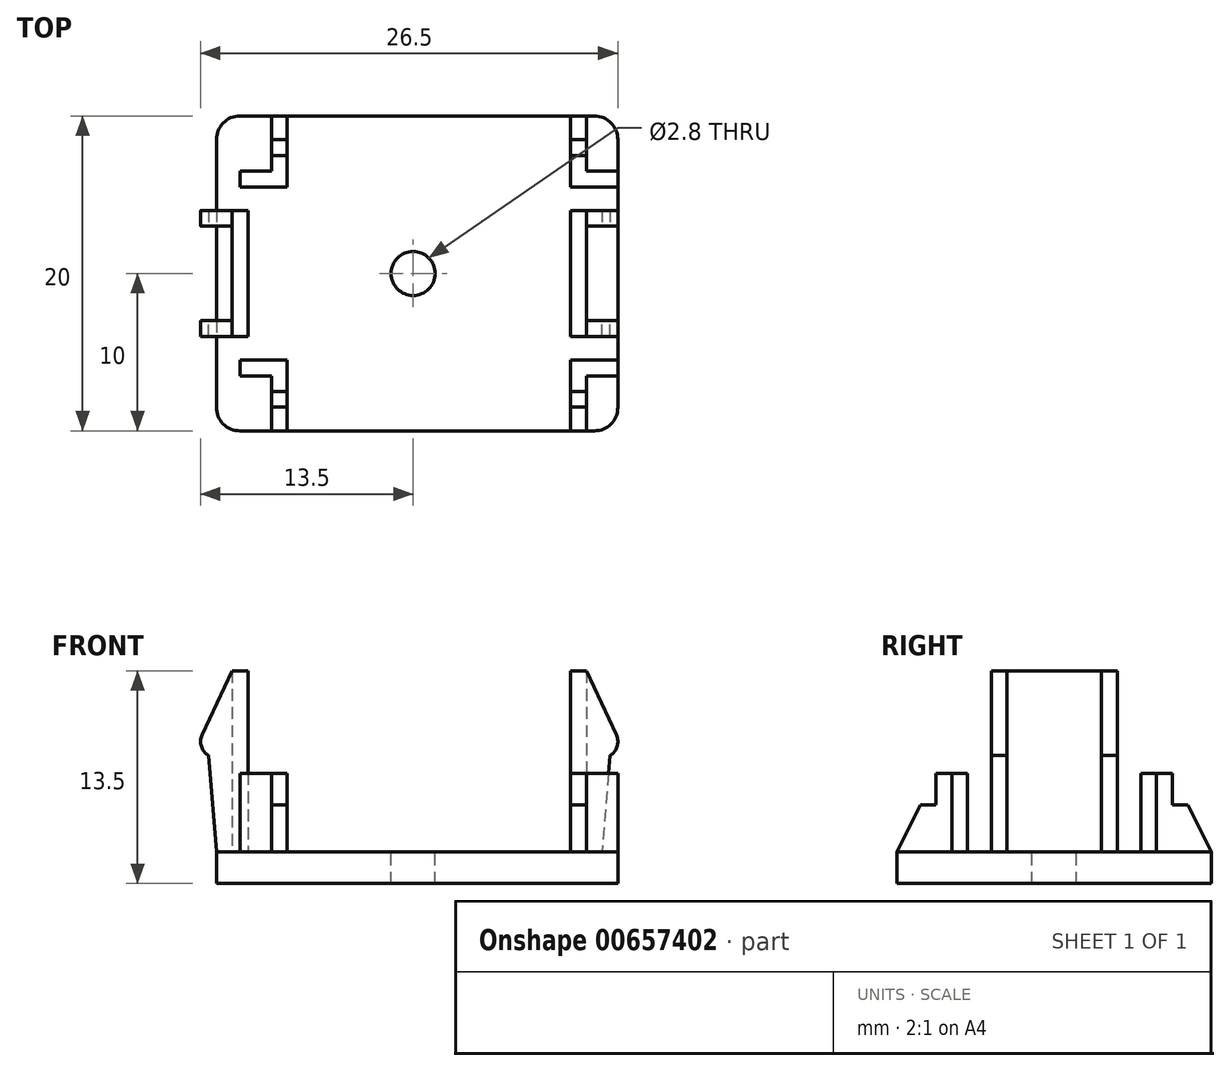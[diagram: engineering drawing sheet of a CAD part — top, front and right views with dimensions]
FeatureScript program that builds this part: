
annotation { "Feature Type Name" : "Feature", "Feature Type Description" : "" }
export const myFeature = defineFeature(function(context is Context, id is Id, definition is map)
    precondition{}
    {
        {
            var Q0;
            Q0=qCreatedBy(makeId("Top.planeOp"),FACE);
            var sketch = newSketch(context, id + "F0", { "sketchPlane" : qUnion([Q0])});
            skLineSegment(sketch, "E0", {"start": v(-7.5, 10) * mm, "end": v(-7.5, 5.5) * mm});
            skLineSegment(sketch, "E1", {"start": v(-7.5, 5.5) * mm, "end": v(-10.5, 5.5) * mm});
            skLineSegment(sketch, "E2", {"start": v(-10.5, 5.5) * mm, "end": v(-10.5, 6.5) * mm});
            skLineSegment(sketch, "E3", {"start": v(-10.5, 6.5) * mm, "end": v(-8.5, 6.5) * mm});
            skLineSegment(sketch, "E4", {"start": v(-8.5, 6.5) * mm, "end": v(-8.5, 10) * mm});
            skLineSegment(sketch, "E5", {"start": v(-8.5, 10) * mm, "end": v(-7.5, 10) * mm});
            skLineSegment(sketch, "E6", {"start": v(-13, 4) * mm, "end": v(-10, 4) * mm});
            skLineSegment(sketch, "E7", {"start": v(-10, 4) * mm, "end": v(-10, 0) * mm});
            skLineSegment(sketch, "E8", {"start": v(-10, 0) * mm, "end": v(-11, 0) * mm});
            skLineSegment(sketch, "E9", {"start": v(-11, 0) * mm, "end": v(-11, 3) * mm});
            skLineSegment(sketch, "E10", {"start": v(-11, 3) * mm, "end": v(-13, 3) * mm});
            skLineSegment(sketch, "E11", {"start": v(-13, 3) * mm, "end": v(-13, 4) * mm});
            skLineSegment(sketch, "E12", {"start": v(10.5, 10) * mm, "end": v(10.5, 5.5) * mm});
            skPoint(sketch, "E12.startSnap0", {"position": v(-8, 10) * mm});
            skLineSegment(sketch, "E13", {"start": v(10.5, 5.5) * mm, "end": v(13.5, 5.5) * mm});
            skLineSegment(sketch, "E14", {"start": v(13.5, 5.5) * mm, "end": v(13.5, 6.5) * mm});
            skLineSegment(sketch, "E15", {"start": v(13.5, 6.5) * mm, "end": v(11.5, 6.5) * mm});
            skLineSegment(sketch, "E16", {"start": v(11.5, 6.5) * mm, "end": v(11.5, 10) * mm});
            skLineSegment(sketch, "E17", {"start": v(11.5, 10) * mm, "end": v(10.5, 10) * mm});
            skLineSegment(sketch, "E18", {"start": v(10.5, 4) * mm, "end": v(10.5, 0) * mm});
            skLineSegment(sketch, "E19", {"start": v(10.5, 0) * mm, "end": v(11.5, 0) * mm});
            skLineSegment(sketch, "E20", {"start": v(11.5, 0) * mm, "end": v(11.5, 3) * mm});
            skLineSegment(sketch, "E21", {"start": v(11.5, 3) * mm, "end": v(13.5, 3) * mm});
            skLineSegment(sketch, "E22", {"start": v(13.5, 3) * mm, "end": v(13.5, 4) * mm});
            skLineSegment(sketch, "E23", {"start": v(13.5, 4) * mm, "end": v(10.5, 4) * mm});
            skSolve(sketch);
        }
        {
            var Q0;
            Q0=makeQuery(id+"F0.imprint","IMPRINT",FACE,{"disambiguationData":[TD([[makeQuery(id+"F0.imprint","IMPRINT",EDGE,{"derivedFrom":sQuery(id+"F0.wireOp",EDGE,"E0")}),-1.0]])]});
            var Q1;
            Q1=makeQuery(id+"F0.imprint","IMPRINT",FACE,{"disambiguationData":[TD([[makeQuery(id+"F0.imprint","IMPRINT",EDGE,{"derivedFrom":sQuery(id+"F0.wireOp",EDGE,"E6")}),-1.0]])]});
            var Q2;
            Q2=makeQuery(id+"F0.imprint","IMPRINT",FACE,{"disambiguationData":[TD([[makeQuery(id+"F0.imprint","IMPRINT",EDGE,{"derivedFrom":sQuery(id+"F0.wireOp",EDGE,"E12")}),1.0]])]});
            var Q3;
            Q3=makeQuery(id+"F0.imprint","IMPRINT",FACE,{"disambiguationData":[TD([[makeQuery(id+"F0.imprint","IMPRINT",EDGE,{"derivedFrom":sQuery(id+"F0.wireOp",EDGE,"E18")}),1.0]])]});
            extrude(context, id + "F1", {"entities" : qUnion([Q0, Q1, Q2, Q3]), "depth" : 11.5 * mm});
        }
        {
            var Q0;
            Q0=makeQuery(id+"F1.opExtrude","SWEPT_FACE",FACE,{"disambiguationData":[OSD([sQuery(id+"F0.wireOp",EDGE,"E10")])]});
            var sketch = newSketch(context, id + "F2", { "sketchPlane" : qUnion([Q0])});
            skArc(sketch, "E24", {"start": v(-12.9, 7.42) * mm, "mid": v(-12.95, 6.7) * mm, "end": v(-12.5, 6.13) * mm});
            skArc(sketch, "E25", {"start": v(13.4, 7.42) * mm, "mid": v(13.45, 6.7) * mm, "end": v(13, 6.13) * mm});
            skLineSegment(sketch, "E26", {"start": v(-12, 0) * mm, "end": v(-12.5, 6.13) * mm});
            skLineSegment(sketch, "E27", {"start": v(-12, 0) * mm, "end": v(-13, 0) * mm});
            skLineSegment(sketch, "E28", {"start": v(-13, 0) * mm, "end": v(-13, 7) * mm});
            skLineSegment(sketch, "E29", {"start": v(-11, 11.5) * mm, "end": v(-12.9, 7.42) * mm});
            skLineSegment(sketch, "E30", {"start": v(-11, 11.5) * mm, "end": v(-13, 11.5) * mm});
            skLineSegment(sketch, "E31", {"start": v(-13, 11.5) * mm, "end": v(-13, 7) * mm});
            skLineSegment(sketch, "E32", {"start": v(12.5, 0) * mm, "end": v(13, 6.13) * mm});
            skLineSegment(sketch, "E33", {"start": v(12.5, 0) * mm, "end": v(13.5, 0) * mm});
            skLineSegment(sketch, "E34", {"start": v(13.5, 0) * mm, "end": v(13.5, 7) * mm});
            skLineSegment(sketch, "E35", {"start": v(11.5, 11.5) * mm, "end": v(13.4, 7.42) * mm});
            skLineSegment(sketch, "E36", {"start": v(11.5, 11.5) * mm, "end": v(13.5, 11.5) * mm});
            skLineSegment(sketch, "E37", {"start": v(13.5, 11.5) * mm, "end": v(13.5, 7) * mm});
            skSolve(sketch);
        }
        {
            var Q0;
            {var subQ0=sQuery(id+"F2.wireOp",EDGE,"E29");Q0=makeQuery(id+"F2.imprint","IMPRINT",FACE,{"disambiguationData":[TD([[makeQuery(id+"F2.imprint","IMPRINT",EDGE,{"derivedFrom":subQ0}),-1.0]])]});}
            var Q1;
            {var subQ0=sQuery(id+"F2.wireOp",EDGE,"E26");Q1=makeQuery(id+"F2.imprint","IMPRINT",FACE,{"disambiguationData":[TD([[makeQuery(id+"F2.imprint","IMPRINT",EDGE,{"derivedFrom":subQ0}),1.0]])]});}
            var Q2;
            {var subQ0=sQuery(id+"F2.wireOp",EDGE,"E35");Q2=makeQuery(id+"F2.imprint","IMPRINT",FACE,{"disambiguationData":[TD([[makeQuery(id+"F2.imprint","IMPRINT",EDGE,{"derivedFrom":subQ0}),1.0]])]});}
            var Q3;
            {var subQ0=sQuery(id+"F2.wireOp",EDGE,"E32");Q3=makeQuery(id+"F2.imprint","IMPRINT",FACE,{"disambiguationData":[TD([[makeQuery(id+"F2.imprint","IMPRINT",EDGE,{"derivedFrom":subQ0}),-1.0]])]});}
            extrude(context, id + "F3", {"entities" : qUnion([Q0, Q1, Q2, Q3]), "operationType" : NewBodyOperationType.REMOVE, "endBound" : BoundingType.UP_TO_NEXT, "oppositeDirection" : true, "depth" : 25 * mm});
        }
        {
            var Q0;
            Q0=makeQuery(id+"F1.opExtrude","SWEPT_BODY",BODY,{"disambiguationData":[OSD([sQuery(id+"F0.wireOp",EDGE,"E6"),sQuery(id+"F0.wireOp",EDGE,"E7"),sQuery(id+"F0.wireOp",EDGE,"E8"),sQuery(id+"F0.wireOp",EDGE,"E9"),sQuery(id+"F0.wireOp",EDGE,"E10"),sQuery(id+"F0.wireOp",EDGE,"E11")])]});
            var Q1;
            Q1=makeQuery(id+"F1.opExtrude","SWEPT_BODY",BODY,{"disambiguationData":[OSD([sQuery(id+"F0.wireOp",EDGE,"E18"),sQuery(id+"F0.wireOp",EDGE,"E19"),sQuery(id+"F0.wireOp",EDGE,"E20"),sQuery(id+"F0.wireOp",EDGE,"E21"),sQuery(id+"F0.wireOp",EDGE,"E22"),sQuery(id+"F0.wireOp",EDGE,"E23")])]});
            var Q2;
            Q2=makeQuery(id+"F1.opExtrude","SWEPT_BODY",BODY,{"disambiguationData":[OSD([sQuery(id+"F0.wireOp",EDGE,"E12"),sQuery(id+"F0.wireOp",EDGE,"E13"),sQuery(id+"F0.wireOp",EDGE,"E14"),sQuery(id+"F0.wireOp",EDGE,"E15"),sQuery(id+"F0.wireOp",EDGE,"E16"),sQuery(id+"F0.wireOp",EDGE,"E17")])]});
            var Q3;
            Q3=makeQuery(id+"F1.opExtrude","SWEPT_BODY",BODY,{"disambiguationData":[OSD([sQuery(id+"F0.wireOp",EDGE,"E0"),sQuery(id+"F0.wireOp",EDGE,"E1"),sQuery(id+"F0.wireOp",EDGE,"E2"),sQuery(id+"F0.wireOp",EDGE,"E3"),sQuery(id+"F0.wireOp",EDGE,"E4"),sQuery(id+"F0.wireOp",EDGE,"E5")])]});
            var Q4;
            Q4=qCreatedBy(makeId("Front.planeOp"),FACE);
            mirror(context, id + "F4", {"operationType" : NewBodyOperationType.ADD, "entities" : qUnion([Q0, Q1, Q2, Q3]), "mirrorPlane" : qUnion([Q4])});
        }
        {
            var Q0;
            Q0=makeQuery(id+"F1.opExtrude","SWEPT_FACE",FACE,{"disambiguationData":[OSD([sQuery(id+"F0.wireOp",EDGE,"E4")])]});
            var sketch = newSketch(context, id + "F5", { "sketchPlane" : qUnion([Q0])});
            skLineSegment(sketch, "E38.bottom", {"start": v(-10, 11.5) * mm, "end": v(-5.5, 11.5) * mm});
            skLineSegment(sketch, "E38.top", {"start": v(-10, 5) * mm, "end": v(-5.5, 5) * mm});
            skLineSegment(sketch, "E38.left", {"start": v(-10, 11.5) * mm, "end": v(-10, 5) * mm});
            skLineSegment(sketch, "E38.right", {"start": v(-5.5, 11.5) * mm, "end": v(-5.5, 5) * mm});
            skLineSegment(sketch, "E39.bottom", {"start": v(10, 11.5) * mm, "end": v(5.5, 11.5) * mm});
            skLineSegment(sketch, "E39.top", {"start": v(10, 5) * mm, "end": v(5.5, 5) * mm});
            skLineSegment(sketch, "E39.left", {"start": v(10, 11.5) * mm, "end": v(10, 5) * mm});
            skLineSegment(sketch, "E39.right", {"start": v(5.5, 11.5) * mm, "end": v(5.5, 5) * mm});
            skSolve(sketch);
        }
        {
            var Q0;
            Q0=qSketchRegion(id+"F5",true);
            extrude(context, id + "F6", {"entities" : qUnion([Q0]), "operationType" : NewBodyOperationType.REMOVE, "endBound" : BoundingType.SYMMETRIC, "oppositeDirection" : true, "depth" : 56.26 * mm});
        }
        {
            var Q0;
            Q0=makeQuery(id+"F1.opExtrude","SWEPT_FACE",FACE,{"disambiguationData":[OSD([sQuery(id+"F0.wireOp",EDGE,"E4")])]});
            var sketch = newSketch(context, id + "F7", { "sketchPlane" : qUnion([Q0])});
            skLineSegment(sketch, "E40", {"start": v(-10, 0) * mm, "end": v(-8.5, 3) * mm});
            skLineSegment(sketch, "E41", {"start": v(-8.5, 3) * mm, "end": v(-7.5, 3) * mm});
            skLineSegment(sketch, "E42", {"start": v(-7.5, 3) * mm, "end": v(-7.5, 5) * mm});
            skLineSegment(sketch, "E43", {"start": v(-7.5, 5) * mm, "end": v(-10, 5) * mm});
            skLineSegment(sketch, "E44", {"start": v(-10, 5) * mm, "end": v(-10, 0) * mm});
            skSolve(sketch);
        }
        {
            var Q0;
            Q0=makeQuery(id+"F7.imprint","IMPRINT",FACE,{"disambiguationData":[TD([[makeQuery(id+"F7.imprint","IMPRINT",EDGE,{"derivedFrom":sQuery(id+"F7.wireOp",EDGE,"E40")}),1.0]])]});
            extrude(context, id + "F8", {"entities" : qUnion([Q0]), "operationType" : NewBodyOperationType.REMOVE, "endBound" : BoundingType.THROUGH_ALL, "oppositeDirection" : true, "depth" : 25 * mm});
        }
        {
            var Q0;
            Q0=makeQuery(id+"F4.opPattern","COPY",FACE,{"derivedFrom":makeQuery(id+"F1.opExtrude","SWEPT_FACE",FACE,{"disambiguationData":[OSD([sQuery(id+"F0.wireOp",EDGE,"E4")])]}),"instanceName":"1"});
            var sketch = newSketch(context, id + "F9", { "sketchPlane" : qUnion([Q0])});
            skLineSegment(sketch, "E45", {"start": v(10, 0) * mm, "end": v(8.5, 3) * mm});
            skLineSegment(sketch, "E46", {"start": v(8.5, 3) * mm, "end": v(7.5, 3) * mm});
            skLineSegment(sketch, "E47", {"start": v(7.5, 3) * mm, "end": v(7.5, 5) * mm});
            skLineSegment(sketch, "E48", {"start": v(7.5, 5) * mm, "end": v(10, 5) * mm});
            skLineSegment(sketch, "E49", {"start": v(10, 5) * mm, "end": v(10, 0) * mm});
            skSolve(sketch);
        }
        {
            var Q0;
            Q0=makeQuery(id+"F9.imprint","IMPRINT",FACE,{"disambiguationData":[TD([[makeQuery(id+"F9.imprint","IMPRINT",EDGE,{"derivedFrom":sQuery(id+"F9.wireOp",EDGE,"E45")}),-1.0]])]});
            extrude(context, id + "F10", {"entities" : qUnion([Q0]), "operationType" : NewBodyOperationType.REMOVE, "endBound" : BoundingType.THROUGH_ALL, "oppositeDirection" : true, "depth" : 25 * mm});
        }
        {
            var Q0;
            Q0=qCreatedBy(makeId("Top.planeOp"),FACE);
            var sketch = newSketch(context, id + "F11", { "sketchPlane" : qUnion([Q0])});
            skLineSegment(sketch, "E50.bottom", {"start": v(-10.5, 10) * mm, "end": v(12, 10) * mm});
            skLineSegment(sketch, "E50.top", {"start": v(-10.5, -10) * mm, "end": v(12, -10) * mm});
            skLineSegment(sketch, "E50.left", {"start": v(-12, 8.5) * mm, "end": v(-12, -8.5) * mm});
            skLineSegment(sketch, "E50.right", {"start": v(13.5, 8.5) * mm, "end": v(13.5, -8.5) * mm});
            skPoint(sketch, "E51.visualSharp", {"position": v(-12, 10) * mm});
            skArc(sketch, "E51.filletArc", {"start": v(-10.5, 10) * mm, "mid": v(-11.56, 9.56) * mm, "end": v(-12, 8.5) * mm});
            skPoint(sketch, "E52.visualSharp", {"position": v(13.5, 10) * mm});
            skArc(sketch, "E52.filletArc", {"start": v(13.5, 8.5) * mm, "mid": v(13.06, 9.56) * mm, "end": v(12, 10) * mm});
            skPoint(sketch, "E53.visualSharp", {"position": v(13.5, -10) * mm});
            skArc(sketch, "E53.filletArc", {"start": v(12, -10) * mm, "mid": v(13.06, -9.56) * mm, "end": v(13.5, -8.5) * mm});
            skPoint(sketch, "E54.visualSharp", {"position": v(-12, -10) * mm});
            skArc(sketch, "E54.filletArc", {"start": v(-12, -8.5) * mm, "mid": v(-11.56, -9.56) * mm, "end": v(-10.5, -10) * mm});
            skCircle(sketch, "E55", {"center": v(0.5, 0) * mm, "radius": 1.4 * mm});
            skSolve(sketch);
        }
        {
            var Q0;
            Q0=makeQuery(id+"F11.imprint","IMPRINT",FACE,{"disambiguationData":[TD([[makeQuery(id+"F11.imprint","IMPRINT",EDGE,{"derivedFrom":sQuery(id+"F11.wireOp",EDGE,"E50.bottom")}),-1.0]])]});
            extrude(context, id + "F12", {"entities" : qUnion([Q0]), "oppositeDirection" : true, "depth" : 2 * mm});
        }
    });
